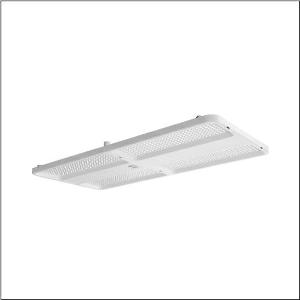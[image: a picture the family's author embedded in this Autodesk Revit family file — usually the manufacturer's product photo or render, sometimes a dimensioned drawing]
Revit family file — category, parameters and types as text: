
# Revit family: highbay_21_maxi_52hn12db4qda01
name_source: partatom
category: Lighting Fixtures
units: mm (PartAtom-declared; Revit-internal decimal feet)

## family parameters
Cut with Voids When Loaded = No
Host = Face
Light Source = No
Part Type = Normal
Room Calculation Point = No
Round Connector Dimension = Use Diameter
Shared = No

## types (1)
- --- (1 x LED, 38000 lm, 198.2 W, 4000K)
    Apparent Load = 198 VA
    CIE Flux Codes = 90 98 100 100 100
    Color Rendering = 80
    Color Temperature = 4000K
    Default Elevation = 1800 mm
    Description = high bay luminaire Highbay 21 maxi; direct symmetric wide distribution, light control with lens of PMMA; UGR ≤ 22 (X = 4H | Y = 8H | S = 0.25H | reflection values 70/50/20); luminous flux: 38.000lm; light colour: 840, colour temperature: 4000K, MacAdam ≤ 3 SDCM (initial), colour rendering: CRI > 80; luminous efficacy: 191,7lm/W; rated service life: 75.000h (L80) at AT= ta max; control: Bluetooth Mesh; for wireless networking: Node multi-sensor luminaire for setting up a local control solution without a higher-level application controller, intelligence completely integrated into the luminaire; with auto-swarm function: leading lighting creates safety. The function is already active without any „out-of-the-box“ commissioning; commissioning is not necessary thanks to „out-of-the-box“ functions: basic functions (presence lighting, follow-up times, fading times, etc.) are already preset at the factory; no control line such as DALI between the Node multi-sensor luminaires and Nodes is required, wireless integration of other Node luminaires and Node multi-sensor luminaires into the network is possible; number of Node multi-sensor luminaires in the project can be expanded as required, network sizes > 300 Nodes can be realized; can also be connected to lighting or building automation via various gateways upon request; integrated DALI2 ECG provides luminaire data (according to IEC62386, Part 251), energy data (Part 252), and monitoring and analytics data (Part 253) to higher-level systems for further processing; luminaire with PIR sensor (passive-infrared); with light sensor; luminaire connection: terminal, 5-pole, max. 2.5mm² (cable entry for one cable, Ø 8.5..16mm); mains connection: 230..240V, AC 50/60Hz; connected load: 198,2W; protection rating (complete): IP65; insulation class (complete): insulation class I (protective earthing); protection symbol: D; certification: CE, UKCA; internal wiring halogen-free; luminaire Suitable for use in the food industry according to the specifications of IFS-Food, HACCP and/or BRC; LABS conformity tested according to VDMA 24364:2018-05; housing frame of high-performance plastic PA6, matt traffic white (RAL 9016); cover of PMMA; dimension (LxWxH): 946 x 442 x 72mm; permissible operating ambient temperature: -20..+40°C (reducing of maximum allowable ambient temperature of 5°C with ceiling mounting); packaging unit: 1 piece; (delivery without accessories; please order mounting accessories separately)
    Height = 72 mm  [stored 0.23622 ft]
    Lamp = 1 x LED
    Lamp Light Flux = 38000 lm
    Lamp Power = 198.2 W
    Lamp count = 1
    Length = 946 mm
    Luminous efficacy = 192 lm/W
    Manufacturer = Siteco
    ModVariant = No
    Model = 52HN12DB4QDA01
    Mounting Place = Ceiling
    Mounting Type = Pendant
    Number of Poles = 1
    OnlyDefault = Yes
    Power Factor = 1
    Product Name = Highbay 21 maxi
    Product group = high bay luminaire
    ProductGroupID = 902
    Protection Class = Protection class I
    Protection Degree = IP 65
    RLX_Detail_Level = 1
    RLX_Emergency_Light_Flux = 0 lm
    RLX_Emergency_Type = 0
    RLX_Emergency_Type_DB = No
    RlxData = <blob elided: 128641 chars, md5=18d9a0b1>
    Socket = socket
    Standby Power = 0 W
    System Light Flux = 38001 lm
    System Power = 198 W
    Type Comments = factory setting: luminous flux: 100 % | dim-lin: 254 | 918 mA
    Type Image = l_1363267.jpg
    URL = http://relux.com
    VarID = @adj_014255
    Voltage = 0 V
    Weight = 0.00 kg
    Width = 442 mm

note: [stored X ft] marks values corroborated as IEEE doubles in the binary element streams (Revit-internal decimal feet)

## geometry (parser evidence)
native form markers: Blend x4, Sweep x9
no freeform markers — native parametric forms only
